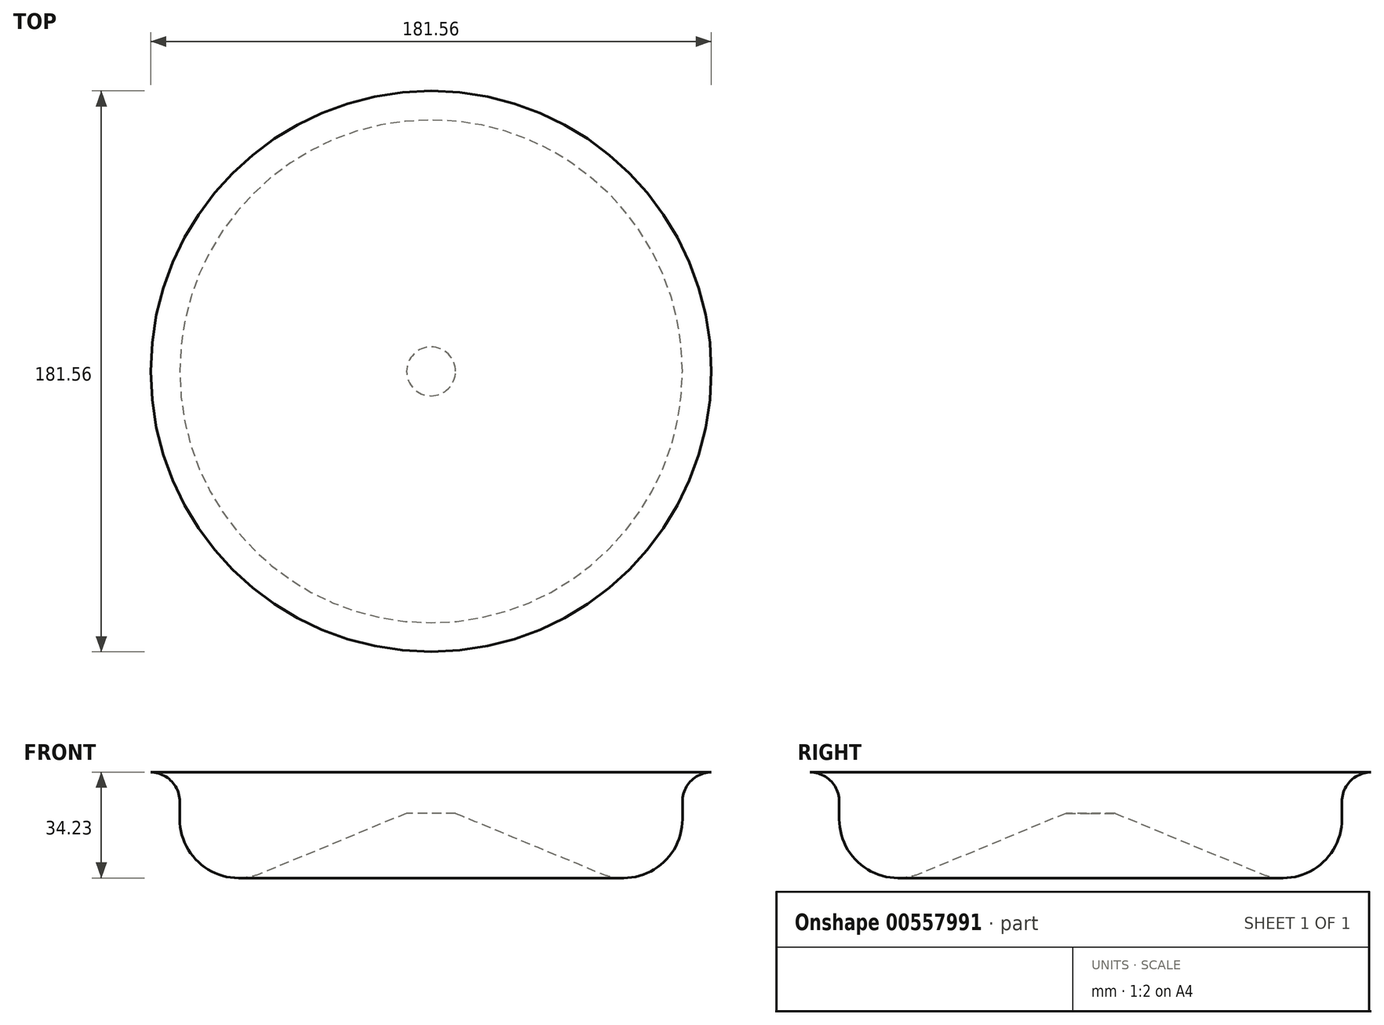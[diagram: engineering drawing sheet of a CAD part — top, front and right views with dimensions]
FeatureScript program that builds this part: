
annotation { "Feature Type Name" : "Feature", "Feature Type Description" : "" }
export const myFeature = defineFeature(function(context is Context, id is Id, definition is map)
    precondition{}
    {
        {
            var Q0;
            Q0=qCreatedBy(makeId("Front.planeOp"),FACE);
            var sketch = newSketch(context, id + "F0", { "sketchPlane" : qUnion([Q0])});
            skLineSegment(sketch, "E0", {"start": v(47.51, 1.32) * mm, "end": v(47.51, -11.94) * mm});
            skLineSegment(sketch, "E1", {"start": v(47.51, -11.94) * mm, "end": v(39.6, -11.94) * mm});
            skLineSegment(sketch, "E2", {"start": v(39.6, -11.94) * mm, "end": v(-7.53, -31.46) * mm});
            skLineSegment(sketch, "E3", {"start": v(-33.87, -8.2) * mm, "end": v(-33.87, -13.86) * mm});
            skArc(sketch, "E4.filletArc", {"start": v(-33.87, -13.86) * mm, "mid": v(-25.4, -29.7) * mm, "end": v(-7.53, -31.46) * mm});
            skArc(sketch, "E5.filletArc", {"start": v(-33.87, -8.2) * mm, "mid": v(-36.7, -1.43) * mm, "end": v(-43.52, 1.32) * mm});
            skLineSegment(sketch, "E6", {"start": v(-43.52, 1.32) * mm, "end": v(47.51, 1.32) * mm});
            skSolve(sketch);
        }
        {
            var Q0;
            {var subQ1=sQuery(id+"F0.wireOp",EDGE,"E0");Q0=makeQuery(id+"F0.imprint","IMPRINT",FACE,{"disambiguationData":[TD([[makeQuery(id+"F0.imprint","IMPRINT",EDGE,{"derivedFrom":subQ1}),-1.0]])]});}
            var Q1;
            Q1=sQuery(id+"F0.wireOp",EDGE,"E0");
            revolve(context, id + "F1", {"entities" : qUnion([Q0]), "axis" : qUnion([Q1]), "revolveType" : RevolveType.FULL});
        }
    });
